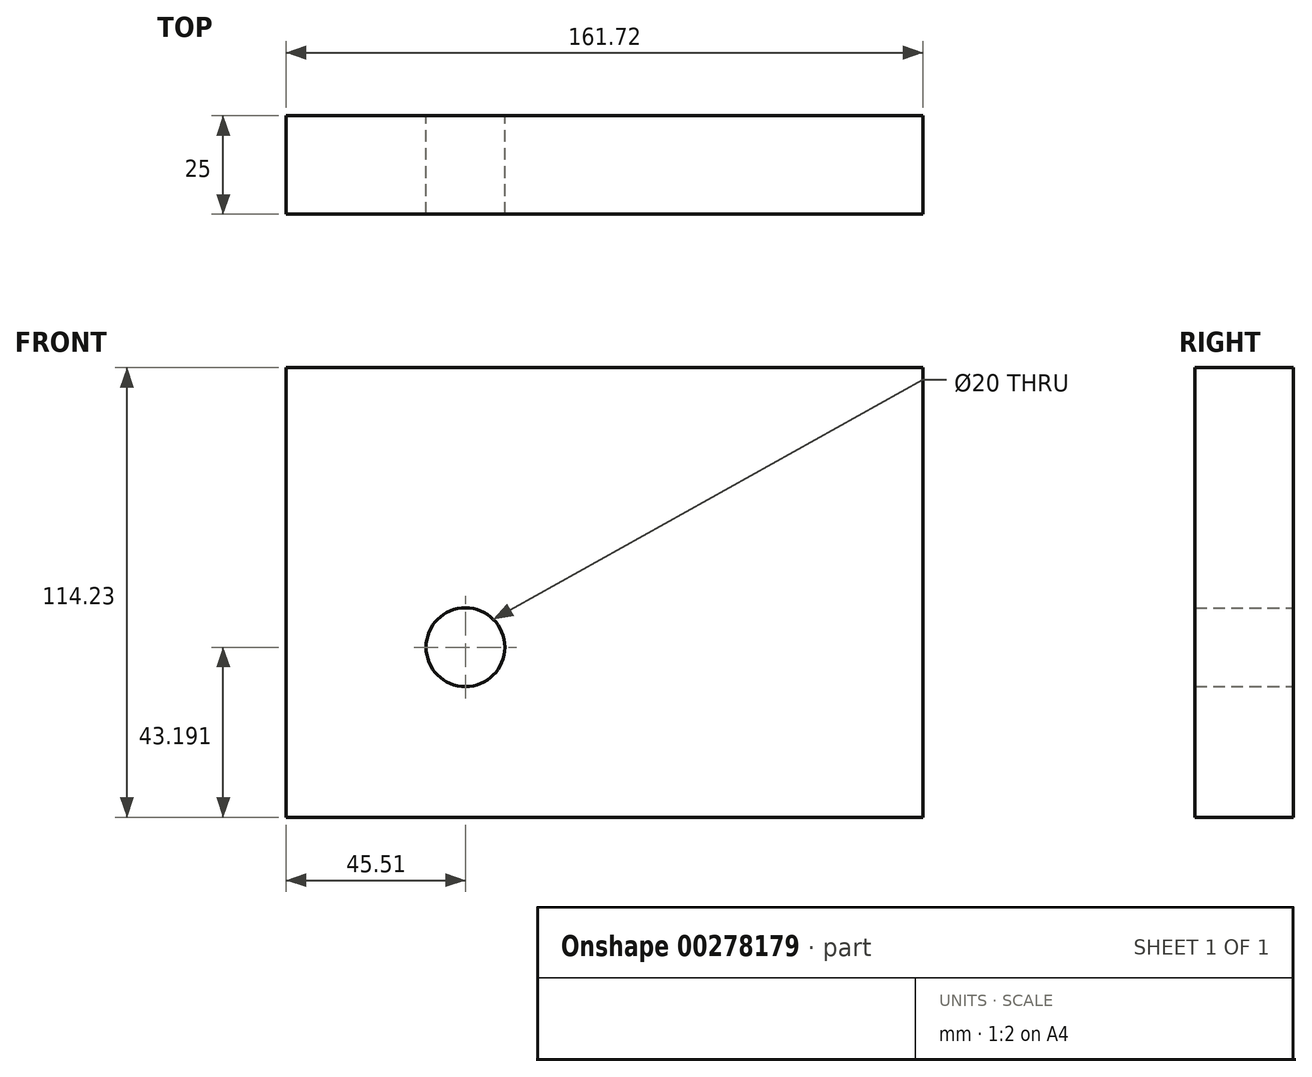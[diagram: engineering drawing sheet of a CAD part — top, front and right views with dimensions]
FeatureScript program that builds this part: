
annotation { "Feature Type Name" : "Feature", "Feature Type Description" : "" }
export const myFeature = defineFeature(function(context is Context, id is Id, definition is map)
    precondition{}
    {
        {
            var Q0;
            Q0=qCreatedBy(makeId("Front.planeOp"),FACE);
            var sketch = newSketch(context, id + "F0", { "sketchPlane" : qUnion([Q0])});
            skLineSegment(sketch, "E0.bottom", {"start": v(0, 0) * mm, "end": v(161.72, 0) * mm});
            skLineSegment(sketch, "E0.top", {"start": v(0, 114.23) * mm, "end": v(161.72, 114.23) * mm});
            skLineSegment(sketch, "E0.left", {"start": v(0, 0) * mm, "end": v(0, 114.23) * mm});
            skLineSegment(sketch, "E0.right", {"start": v(161.72, 0) * mm, "end": v(161.72, 114.23) * mm});
            skCircle(sketch, "E1", {"center": v(45.5, 43.2) * mm, "radius": 10 * mm});
            skSolve(sketch);
        }
        {
            var Q0;
            Q0 = qSketchRegion(id + "F0", true);
            extrude(context, id + "F1", {"entities" : qUnion([Q0]), "depth" : 25 * mm});
        }
    });
